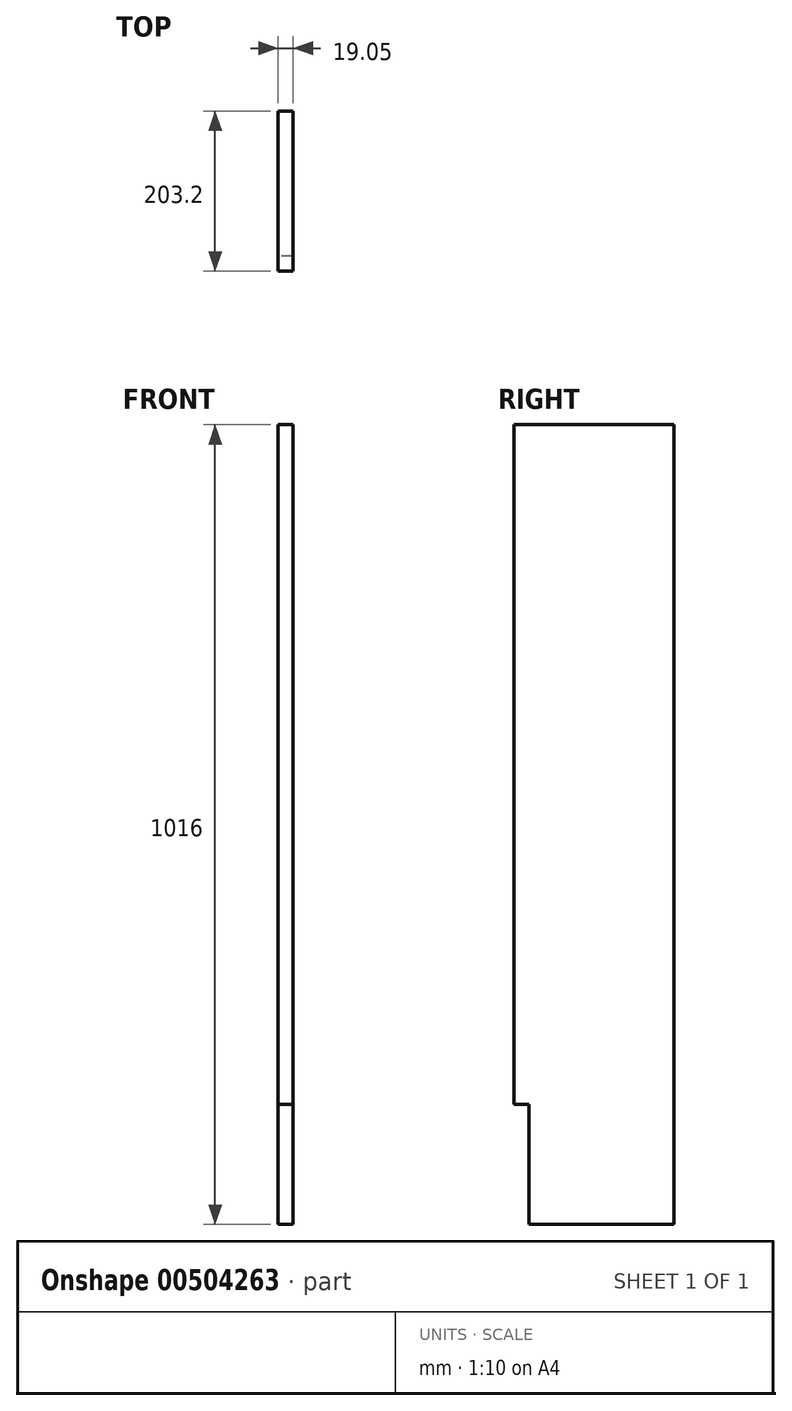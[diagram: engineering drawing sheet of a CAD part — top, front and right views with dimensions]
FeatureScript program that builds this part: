
annotation { "Feature Type Name" : "Feature", "Feature Type Description" : "" }
export const myFeature = defineFeature(function(context is Context, id is Id, definition is map)
    precondition{}
    {
        {
            var Q0;
            Q0=qCreatedBy(makeId("Right.planeOp"),FACE);
            var sketch = newSketch(context, id + "F0", { "sketchPlane" : qUnion([Q0])});
            skLineSegment(sketch, "E0.bottom", {"start": v(101.6, -508) * mm, "end": v(-101.6, -508) * mm});
            skLineSegment(sketch, "E0.top", {"start": v(101.6, 508) * mm, "end": v(-101.6, 508) * mm});
            skLineSegment(sketch, "E0.left", {"start": v(101.6, -508) * mm, "end": v(101.6, 508) * mm});
            skLineSegment(sketch, "E0.right", {"start": v(-101.6, -508) * mm, "end": v(-101.6, 508) * mm});
            skPoint(sketch, "E0.middle", {"position": v(0, 0) * mm});
            skLineSegment(sketch, "E1.bottom", {"start": v(-101.6, -508) * mm, "end": v(-82.55, -508) * mm});
            skLineSegment(sketch, "E1.top", {"start": v(-101.6, -355.6) * mm, "end": v(-82.55, -355.6) * mm});
            skLineSegment(sketch, "E1.left", {"start": v(-101.6, -508) * mm, "end": v(-101.6, -355.6) * mm});
            skLineSegment(sketch, "E1.right", {"start": v(-82.55, -508) * mm, "end": v(-82.55, -355.6) * mm});
            skSolve(sketch);
        }
        {
            var Q0;
            {var subQ1=sQuery(id+"F0.wireOp",EDGE,"E0.top");Q0=makeQuery(id+"F0.imprint","IMPRINT",FACE,{"disambiguationData":[TD([[makeQuery(id+"F0.imprint","IMPRINT",EDGE,{"derivedFrom":subQ1}),1.0]])]});}
            extrude(context, id + "F1", {"entities" : qUnion([Q0]), "depth" : 19.05 * mm});
        }
    });
